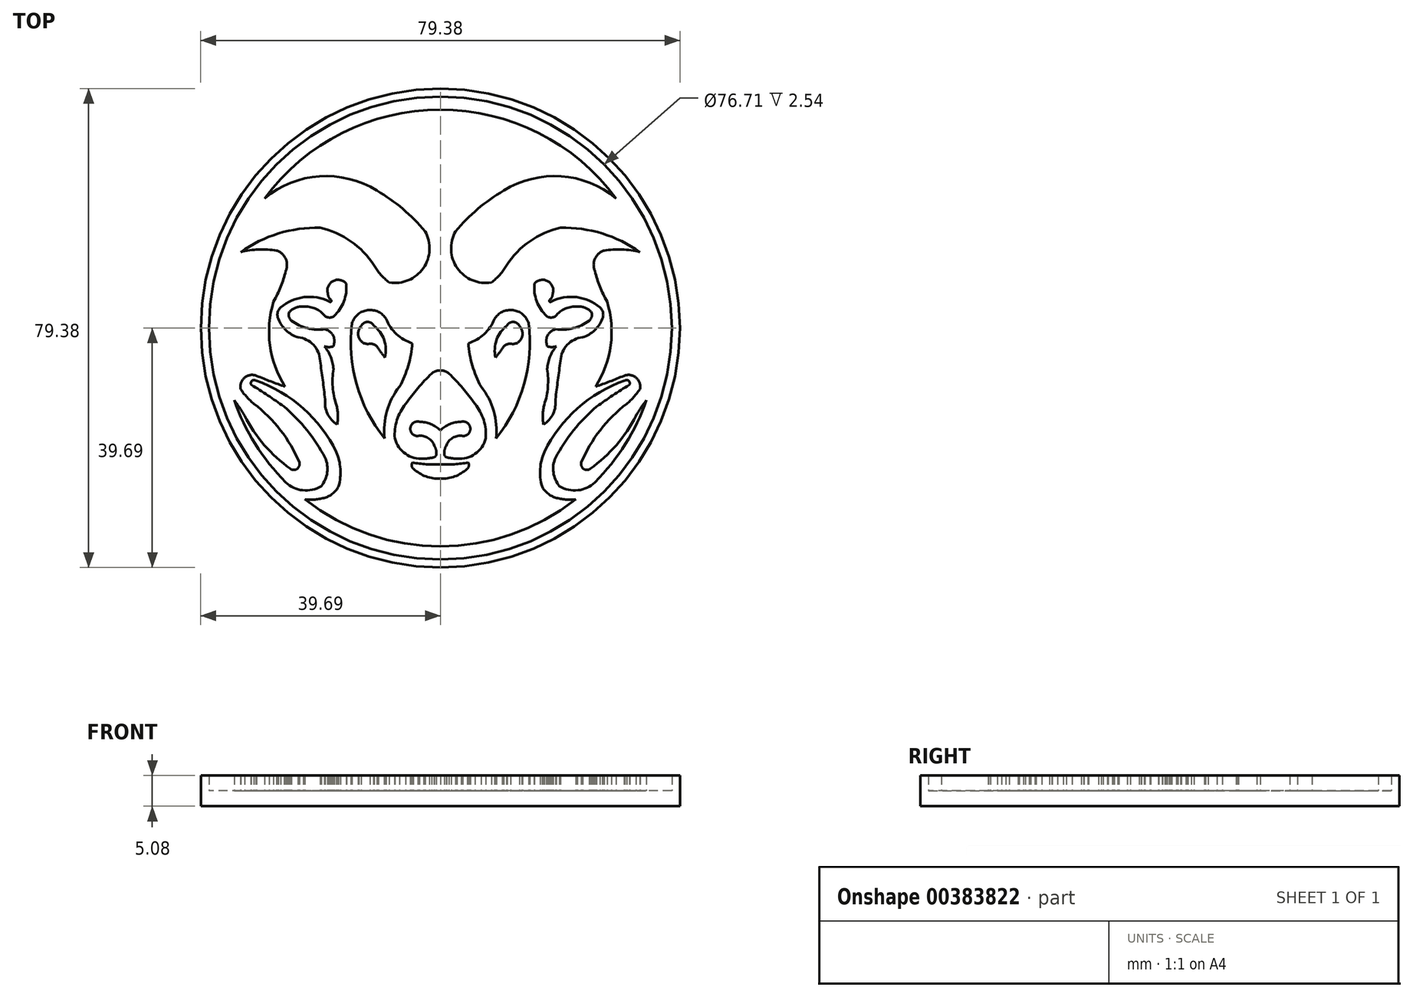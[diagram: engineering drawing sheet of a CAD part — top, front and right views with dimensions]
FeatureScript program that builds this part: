
annotation { "Feature Type Name" : "Feature", "Feature Type Description" : "" }
export const myFeature = defineFeature(function(context is Context, id is Id, definition is map)
    precondition{}
    {
        {
            var Q0;
            Q0=qCreatedBy(makeId("Top.planeOp"),FACE);
            var sketch = newSketch(context, id + "F0", { "sketchPlane" : qUnion([Q0])});
            skCircle(sketch, "E0", {"center": v(0, 0) * mm, "radius": 39.69 * mm});
            skLineSegment(sketch, "E1.bottom", {"start": v(39.69, 39.69) * mm, "end": v(-39.69, 39.69) * mm});
            skLineSegment(sketch, "E1.top", {"start": v(39.69, -39.69) * mm, "end": v(-39.69, -39.69) * mm});
            skLineSegment(sketch, "E1.left", {"start": v(39.69, 39.69) * mm, "end": v(39.69, -39.69) * mm});
            skLineSegment(sketch, "E1.right", {"start": v(-39.69, 39.69) * mm, "end": v(-39.69, -39.69) * mm});
            skCircle(sketch, "E2", {"center": v(0, 0) * mm, "radius": 38.35 * mm});
            skArc(sketch, "E3", {"start": v(29.12, 21.5) * mm, "mid": v(-35.8, -5.4) * mm, "end": v(34.16, -11.96) * mm});
            skArc(sketch, "E4", {"start": v(29.12, 21.5) * mm, "mid": v(20.01, 25.15) * mm, "end": v(10.5, 22.77) * mm});
            skArc(sketch, "E5", {"start": v(10.5, 22.77) * mm, "mid": v(6.22, 19.75) * mm, "end": v(2.52, 16.03) * mm});
            skArc(sketch, "E6", {"start": v(2.52, 16.03) * mm, "mid": v(2.82, 9.92) * mm, "end": v(8.47, 7.56) * mm});
            skArc(sketch, "E7", {"start": v(8.47, 7.56) * mm, "mid": v(9.86, 8.83) * mm, "end": v(10.97, 10.36) * mm});
            skArc(sketch, "E8", {"start": v(19.9, 16.62) * mm, "mid": v(14.82, 14.38) * mm, "end": v(10.97, 10.36) * mm});
            skArc(sketch, "E9", {"start": v(33.07, 12.6) * mm, "mid": v(26.81, 15.67) * mm, "end": v(19.9, 16.62) * mm});
            skArc(sketch, "E10", {"start": v(33.07, 12.6) * mm, "mid": v(30.1, 13.02) * mm, "end": v(27.12, 12.84) * mm});
            skArc(sketch, "E11", {"start": v(27.12, 12.84) * mm, "mid": v(25.62, 11.47) * mm, "end": v(25.61, 9.44) * mm});
            skArc(sketch, "E12", {"start": v(25.61, 9.44) * mm, "mid": v(26.44, 6.85) * mm, "end": v(27.62, 4.4) * mm});
            skArc(sketch, "E13", {"start": v(25.73, -9.71) * mm, "mid": v(28.23, -2.87) * mm, "end": v(27.62, 4.4) * mm});
            skArc(sketch, "E14", {"start": v(25.73, -9.71) * mm, "mid": v(28.1, -8.85) * mm, "end": v(30.42, -7.91) * mm});
            skArc(sketch, "E15", {"start": v(33.06, -10.18) * mm, "mid": v(32.44, -8.24) * mm, "end": v(30.42, -7.91) * mm});
            skArc(sketch, "E16", {"start": v(30.88, -12.56) * mm, "mid": v(32.05, -11.44) * mm, "end": v(33.06, -10.18) * mm});
            skArc(sketch, "E17", {"start": v(30.88, -12.56) * mm, "mid": v(26.48, -16.93) * mm, "end": v(23.37, -22.29) * mm});
            skArc(sketch, "E18", {"start": v(23.37, -22.29) * mm, "mid": v(23.73, -23.34) * mm, "end": v(24.84, -23.33) * mm});
            skArc(sketch, "E19", {"start": v(24.84, -23.33) * mm, "mid": v(29.16, -19.4) * mm, "end": v(32.42, -14.55) * mm});
            skArc(sketch, "E20", {"start": v(34.16, -11.96) * mm, "mid": v(33.24, -13.22) * mm, "end": v(32.42, -14.55) * mm});
            skArc(sketch, "E21", {"start": v(1.44, -7.55) * mm, "mid": v(0.77, -7.15) * mm, "end": v(0, -7.03) * mm});
            skArc(sketch, "E22", {"start": v(5.75, -12.56) * mm, "mid": v(3.7, -9.96) * mm, "end": v(1.44, -7.55) * mm});
            skArc(sketch, "E23", {"start": v(7.54, -18.3) * mm, "mid": v(7.18, -15.26) * mm, "end": v(5.75, -12.56) * mm});
            skArc(sketch, "E24", {"start": v(2.77, -21.66) * mm, "mid": v(5.77, -20.85) * mm, "end": v(7.54, -18.3) * mm});
            skArc(sketch, "E25", {"start": v(1.02, -21.43) * mm, "mid": v(1.9, -21.58) * mm, "end": v(2.77, -21.66) * mm});
            skArc(sketch, "E26", {"start": v(0.65, -20.72) * mm, "mid": v(0.72, -21.14) * mm, "end": v(1.02, -21.43) * mm});
            skArc(sketch, "E27", {"start": v(0.96, -19.57) * mm, "mid": v(0.73, -20.12) * mm, "end": v(0.65, -20.72) * mm});
            skArc(sketch, "E28", {"start": v(3.73, -17.9) * mm, "mid": v(2.03, -18.21) * mm, "end": v(0.96, -19.57) * mm});
            skArc(sketch, "E29", {"start": v(3.73, -17.9) * mm, "mid": v(4.96, -16.56) * mm, "end": v(3.45, -15.54) * mm});
            skArc(sketch, "E30", {"start": v(3.45, -15.54) * mm, "mid": v(1.59, -15.92) * mm, "end": v(0, -16.97) * mm});
            skArc(sketch, "E31", {"start": v(0, -22.62) * mm, "mid": v(2.32, -22.58) * mm, "end": v(4.63, -22.29) * mm});
            skArc(sketch, "E32", {"start": v(4.46, -23.33) * mm, "mid": v(4.73, -22.84) * mm, "end": v(4.63, -22.29) * mm});
            skArc(sketch, "E33", {"start": v(0, -24.97) * mm, "mid": v(2.4, -24.6) * mm, "end": v(4.46, -23.33) * mm});
            skArc(sketch, "E34", {"start": v(19.74, -26.22) * mm, "mid": v(22.9, -26.88) * mm, "end": v(25.77, -25.42) * mm});
            skArc(sketch, "E35", {"start": v(19.08, -21.5) * mm, "mid": v(18.74, -23.96) * mm, "end": v(19.74, -26.22) * mm});
            skArc(sketch, "E36", {"start": v(25.9, -13.02) * mm, "mid": v(22.1, -16.95) * mm, "end": v(19.08, -21.5) * mm});
            skArc(sketch, "E37", {"start": v(31.33, -9.42) * mm, "mid": v(28.57, -11.16) * mm, "end": v(25.9, -13.02) * mm});
            skArc(sketch, "E38", {"start": v(31.33, -9.42) * mm, "mid": v(31.22, -8.76) * mm, "end": v(30.55, -8.7) * mm});
            skArc(sketch, "E39", {"start": v(30.55, -8.7) * mm, "mid": v(22.73, -13.32) * mm, "end": v(17.22, -20.55) * mm});
            skArc(sketch, "E40", {"start": v(17.22, -20.55) * mm, "mid": v(16.56, -23.35) * mm, "end": v(16.83, -26.22) * mm});
            skArc(sketch, "E41", {"start": v(16.83, -26.22) * mm, "mid": v(17.76, -27.4) * mm, "end": v(19.08, -28.12) * mm});
            skArc(sketch, "E42", {"start": v(19.08, -28.12) * mm, "mid": v(20.74, -28.42) * mm, "end": v(22.43, -28.4) * mm});
            skArc(sketch, "E43", {"start": v(4.64, -2.51) * mm, "mid": v(7.27, -1) * mm, "end": v(8.96, 1.5) * mm});
            skArc(sketch, "E44", {"start": v(14.63, 0.8) * mm, "mid": v(12.02, 2.97) * mm, "end": v(8.96, 1.5) * mm});
            skArc(sketch, "E45", {"start": v(9.23, -18.3) * mm, "mid": v(13.88, -9.3) * mm, "end": v(14.63, 0.8) * mm});
            skArc(sketch, "E46", {"start": v(4.64, -2.51) * mm, "mid": v(5.3, -6.23) * mm, "end": v(6.76, -9.73) * mm});
            skArc(sketch, "E47", {"start": v(9.23, -18.3) * mm, "mid": v(8.85, -13.76) * mm, "end": v(6.76, -9.73) * mm});
            skArc(sketch, "E48", {"start": v(18.62, 5.66) * mm, "mid": v(17.8, 7.77) * mm, "end": v(15.58, 7.35) * mm});
            skArc(sketch, "E49", {"start": v(15.58, 7.35) * mm, "mid": v(15.98, 4.43) * mm, "end": v(17.6, 1.98) * mm});
            skArc(sketch, "E50", {"start": v(17.6, 1.98) * mm, "mid": v(18.34, 1.74) * mm, "end": v(19.08, 1.98) * mm});
            skArc(sketch, "E51", {"start": v(22.73, 3.55) * mm, "mid": v(20.71, 3.22) * mm, "end": v(19.08, 1.98) * mm});
            skArc(sketch, "E52", {"start": v(24.98, 2.72) * mm, "mid": v(23.95, 3.38) * mm, "end": v(22.73, 3.55) * mm});
            skArc(sketch, "E53", {"start": v(24.66, 1.22) * mm, "mid": v(25.1, 1.9) * mm, "end": v(24.98, 2.72) * mm});
            skArc(sketch, "E54", {"start": v(19.08, -0.2) * mm, "mid": v(22, -0.03) * mm, "end": v(24.66, 1.22) * mm});
            skArc(sketch, "E55", {"start": v(19.08, -0.2) * mm, "mid": v(18.15, -0.74) * mm, "end": v(17.6, -1.66) * mm});
            skArc(sketch, "E56", {"start": v(17.6, -1.66) * mm, "mid": v(17.58, -2.36) * mm, "end": v(17.7, -3.04) * mm});
            skArc(sketch, "E57", {"start": v(17.7, -3.04) * mm, "mid": v(18.45, -3.16) * mm, "end": v(19.2, -3.04) * mm});
            skArc(sketch, "E58", {"start": v(19.2, -3.04) * mm, "mid": v(18.15, -4.8) * mm, "end": v(17.7, -6.81) * mm});
            skArc(sketch, "E59", {"start": v(17.22, -12.69) * mm, "mid": v(17.82, -9.78) * mm, "end": v(17.7, -6.81) * mm});
            skArc(sketch, "E60", {"start": v(17.22, -12.69) * mm, "mid": v(16.98, -14.34) * mm, "end": v(17.1, -16.01) * mm});
            skArc(sketch, "E61", {"start": v(17.1, -16.01) * mm, "mid": v(18.69, -14.2) * mm, "end": v(19.08, -11.82) * mm});
            skArc(sketch, "E62", {"start": v(19.92, -5.44) * mm, "mid": v(19.48, -8.63) * mm, "end": v(19.08, -11.82) * mm});
            skArc(sketch, "E63", {"start": v(23.6, -1.53) * mm, "mid": v(21.02, -2.8) * mm, "end": v(19.92, -5.44) * mm});
            skArc(sketch, "E64", {"start": v(23.6, -1.53) * mm, "mid": v(25.56, -0.38) * mm, "end": v(26.84, 1.5) * mm});
            skArc(sketch, "E65", {"start": v(26.84, 1.5) * mm, "mid": v(26.96, 2.53) * mm, "end": v(26.46, 3.43) * mm});
            skArc(sketch, "E66", {"start": v(26.46, 3.43) * mm, "mid": v(22.56, 5.12) * mm, "end": v(18.37, 4.39) * mm});
            skArc(sketch, "E67", {"start": v(18.1, 4.65) * mm, "mid": v(18.47, 5.1) * mm, "end": v(18.62, 5.66) * mm});
            skArc(sketch, "E68", {"start": v(18.1, 4.65) * mm, "mid": v(18.1, 4.38) * mm, "end": v(18.37, 4.39) * mm});
            skArc(sketch, "E69", {"start": v(13.09, 0.36) * mm, "mid": v(12.1, 1) * mm, "end": v(11.05, 0.44) * mm});
            skArc(sketch, "E70", {"start": v(13.5, -1.6) * mm, "mid": v(13.58, -0.56) * mm, "end": v(13.09, 0.36) * mm});
            skArc(sketch, "E71", {"start": v(11.65, -2.6) * mm, "mid": v(12.77, -2.45) * mm, "end": v(13.5, -1.6) * mm});
            skArc(sketch, "E72", {"start": v(11.65, -2.6) * mm, "mid": v(10.83, -2.8) * mm, "end": v(10.26, -3.42) * mm});
            skArc(sketch, "E73", {"start": v(9.15, -4.9) * mm, "mid": v(9.72, -4.17) * mm, "end": v(10.26, -3.42) * mm});
            skArc(sketch, "E74", {"start": v(11.05, 0.44) * mm, "mid": v(9.32, -1.96) * mm, "end": v(9.15, -4.9) * mm});
            skLineSegment(sketch, "E75", {"start": v(0, -7.03) * mm, "end": v(0, -16.97) * mm});
            skLineSegment(sketch, "E76", {"start": v(0, -22.62) * mm, "end": v(0, -24.97) * mm});
            skLineSegment(sketch, "E77", {"start": v(0, 0) * mm, "end": v(0, 36.2) * mm});
            skLineSegment(sketch, "E78", {"start": v(0, 0) * mm, "end": v(0, -36.2) * mm});
            skSolve(sketch);
        }
        {
            var Q0;
            Q0=makeQuery(id+"F0.imprint","IMPRINT",FACE,{"disambiguationData":[TD([[makeQuery(id+"F0.imprint","IMPRINT",EDGE,{"derivedFrom":sQuery(id+"F0.wireOp",EDGE,"E2")}),1.0]])]});
            var Q1;
            Q1=makeQuery(id+"F0.imprint","IMPRINT",FACE,{"disambiguationData":[TD([[makeQuery(id+"F0.imprint","IMPRINT",EDGE,{"derivedFrom":sQuery(id+"F0.wireOp",EDGE,"E43")}),-1.0]])]});
            var Q2;
            Q2=makeQuery(id+"F0.imprint","IMPRINT",FACE,{"disambiguationData":[TD([[makeQuery(id+"F0.imprint","IMPRINT",EDGE,{"derivedFrom":sQuery(id+"F0.wireOp",EDGE,"E48")}),1.0]])]});
            var Q3;
            Q3=makeQuery(id+"F0.imprint","IMPRINT",FACE,{"disambiguationData":[TD([[makeQuery(id+"F0.imprint","IMPRINT",EDGE,{"derivedFrom":sQuery(id+"F0.wireOp",EDGE,"E21")}),1.0]])]});
            var Q4;
            Q4=makeQuery(id+"F0.imprint","IMPRINT",FACE,{"disambiguationData":[TD([[makeQuery(id+"F0.imprint","IMPRINT",EDGE,{"derivedFrom":sQuery(id+"F0.wireOp",EDGE,"E31")}),-1.0]])]});
            var Q5;
            {var subQ0=sQuery(id+"F0.wireOp",EDGE,"E35");Q5=makeQuery(id+"F0.imprint","IMPRINT",FACE,{"disambiguationData":[TD([[makeQuery(id+"F0.imprint","IMPRINT",EDGE,{"derivedFrom":subQ0}),-1.0]])]});}
            extrude(context, id + "F1", {"entities" : qUnion([Q0, Q1, Q2, Q3, Q4, Q5]), "depth" : 2.54 * mm});
        }
        {
            var Q0;
            {var subQ8=sQuery(id+"F0.wireOp",EDGE,"E4");Q0=makeQuery(id+"F0.imprint","IMPRINT",FACE,{"disambiguationData":[TD([[makeQuery(id+"F0.imprint","IMPRINT",EDGE,{"derivedFrom":subQ8}),-1.0]])]});}
            var Q1;
            Q1=makeQuery(id+"F0.imprint","IMPRINT",FACE,{"disambiguationData":[TD([[makeQuery(id+"F0.imprint","IMPRINT",EDGE,{"derivedFrom":sQuery(id+"F0.wireOp",EDGE,"E2")}),-1.0]])]});
            var Q2;
            Q2=makeQuery(id+"F0.imprint","IMPRINT",FACE,{"disambiguationData":[TD([[makeQuery(id+"F0.imprint","IMPRINT",EDGE,{"derivedFrom":sQuery(id+"F0.wireOp",EDGE,"E69")}),1.0]])]});
            extrude(context, id + "F2", {"entities" : qUnion([Q0, Q1, Q2]), "operationType" : NewBodyOperationType.ADD, "depth" : 5.08 * mm});
        }
        {
            var Q0;
            Q0=makeQuery(id+"F1.opExtrude","SWEPT_BODY",BODY,{"disambiguationData":[OSD([sQuery(id+"F0.wireOp",EDGE,"E2"),sQuery(id+"F0.wireOp",EDGE,"E3"),sQuery(id+"F0.wireOp",EDGE,"E4"),sQuery(id+"F0.wireOp",EDGE,"E5"),sQuery(id+"F0.wireOp",EDGE,"E6"),sQuery(id+"F0.wireOp",EDGE,"E7"),sQuery(id+"F0.wireOp",EDGE,"E8"),sQuery(id+"F0.wireOp",EDGE,"E9"),sQuery(id+"F0.wireOp",EDGE,"E10"),sQuery(id+"F0.wireOp",EDGE,"E11"),sQuery(id+"F0.wireOp",EDGE,"E12"),sQuery(id+"F0.wireOp",EDGE,"E13"),sQuery(id+"F0.wireOp",EDGE,"E14"),sQuery(id+"F0.wireOp",EDGE,"E15"),sQuery(id+"F0.wireOp",EDGE,"E16"),sQuery(id+"F0.wireOp",EDGE,"E17"),sQuery(id+"F0.wireOp",EDGE,"E18"),sQuery(id+"F0.wireOp",EDGE,"E19"),sQuery(id+"F0.wireOp",EDGE,"E20"),sQuery(id+"F0.wireOp",EDGE,"E34"),sQuery(id+"F0.wireOp",EDGE,"E35"),sQuery(id+"F0.wireOp",EDGE,"E36"),sQuery(id+"F0.wireOp",EDGE,"E37"),sQuery(id+"F0.wireOp",EDGE,"E38"),sQuery(id+"F0.wireOp",EDGE,"E39"),sQuery(id+"F0.wireOp",EDGE,"E40"),sQuery(id+"F0.wireOp",EDGE,"E41"),sQuery(id+"F0.wireOp",EDGE,"E42")])]});
            var Q1;
            Q1=qCreatedBy(makeId("Right.planeOp"),FACE);
            mirror(context, id + "F3", {"operationType" : NewBodyOperationType.ADD, "entities" : qUnion([Q0]), "mirrorPlane" : qUnion([Q1])});
        }
    });
